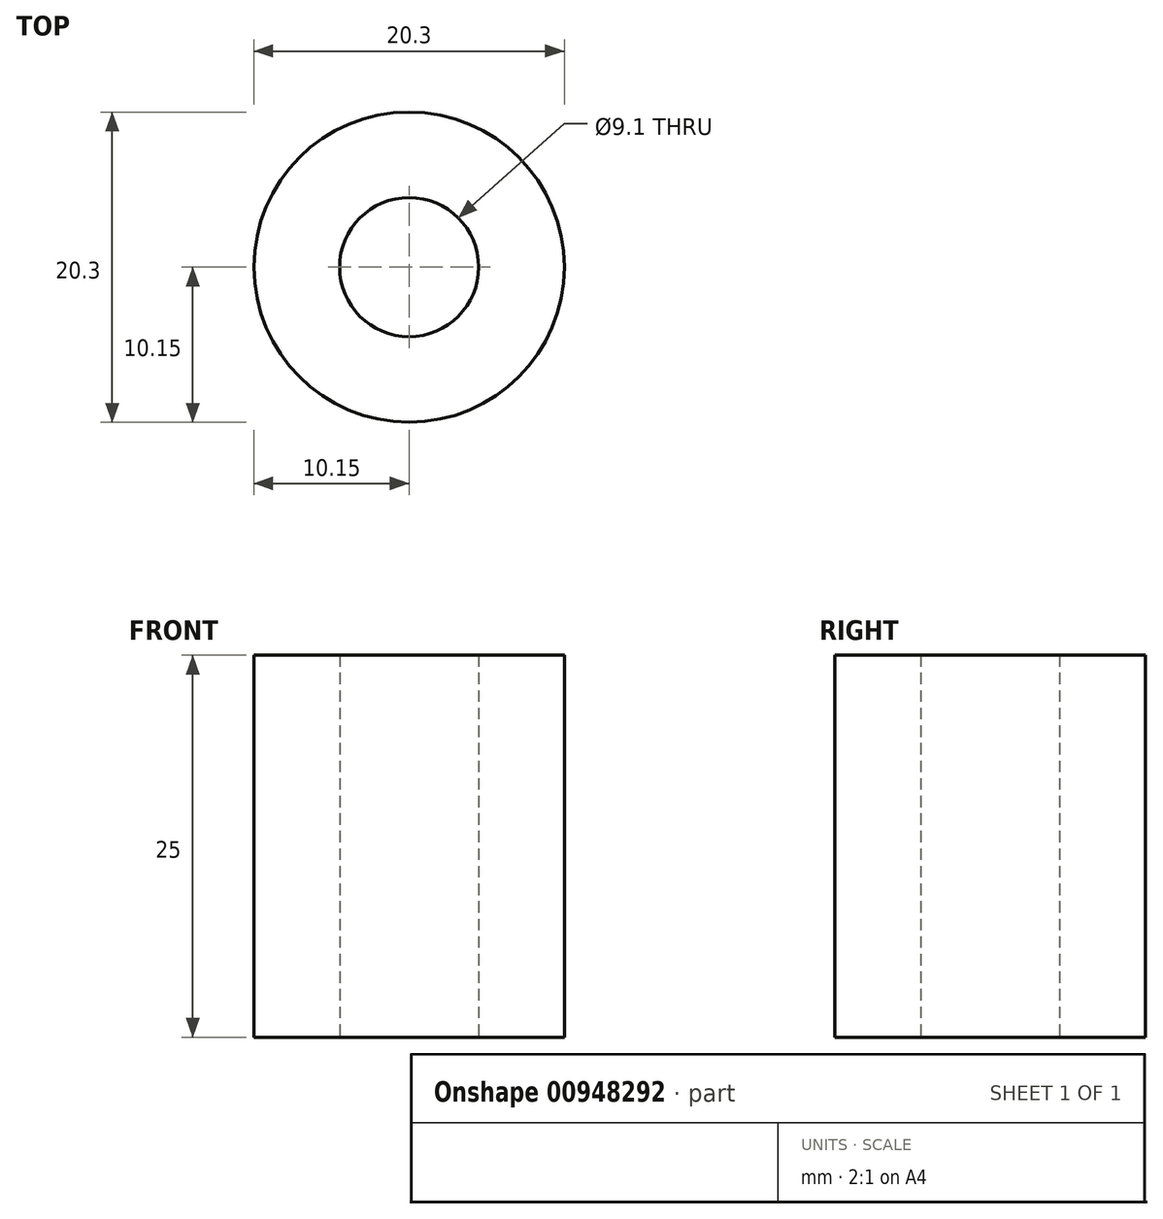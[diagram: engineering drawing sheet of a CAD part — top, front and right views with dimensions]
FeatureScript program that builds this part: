
annotation { "Feature Type Name" : "Feature", "Feature Type Description" : "" }
export const myFeature = defineFeature(function(context is Context, id is Id, definition is map)
    precondition{}
    {
        {
            var Q0;
            Q0=qCreatedBy(makeId("Top.planeOp"),FACE);
            var sketch = newSketch(context, id + "F0", { "sketchPlane" : qUnion([Q0])});
            skCircle(sketch, "E0", {"center": v(0, 0) * mm, "radius": 4.55 * mm});
            skCircle(sketch, "E1", {"center": v(0, 0) * mm, "radius": 10.15 * mm});
            skSolve(sketch);
        }
        {
            var Q0;
            Q0=makeQuery(id+"F0.imprint","IMPRINT",FACE,{"disambiguationData":[TD([[makeQuery(id+"F0.imprint","IMPRINT",EDGE,{"derivedFrom":sQuery(id+"F0.wireOp",EDGE,"E0")}),-1.0]])]});
            extrude(context, id + "F1", {"entities" : qUnion([Q0]), "depth" : 25 * mm, "offsetDistance" : 25 * mm});
        }
    });
